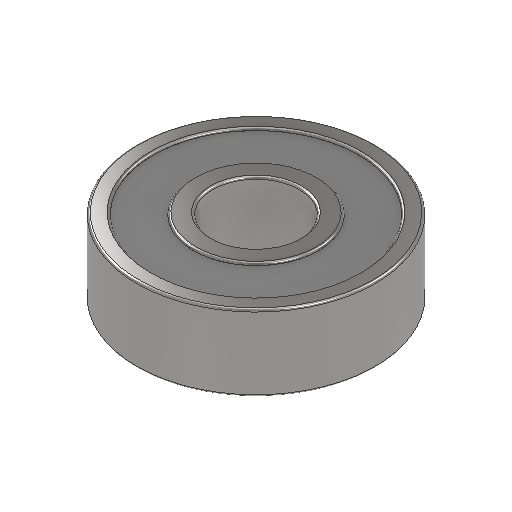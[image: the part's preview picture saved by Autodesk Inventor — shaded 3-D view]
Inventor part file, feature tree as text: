
AUTODESK INVENTOR PART (.ipt)
format: ipt  version: 2025 (Build 290162000, 162)  size: 207,360 bytes
history: native  units: in
note: dims shown in document units (in); Inventor stores cm internally (conversion verified against a paired STEP export)
features: extrude x2, fillet x2, sketch x2, plane x1, mirror x1, projected_geometry x1
ambient origin geometry x8: Origin, YZ Plane, XZ Plane, XY Plane, X Axis, Y Axis, Z Axis, Center Point
bodies: Solid1 (feature_tree)
feature tree (9):
  extrude  "Extrusion1"  Depth=0.315in
  extrude  "Extrusion2"  Depth=0.0079in
  fillet  "Fillet1"  Radius=0.4528in
  plane  "Work Plane1"
  mirror  "Mirror2"
  fillet  "Fillet2"  Radius=0.0083in
  sketch  "Sketch1"  dims[d0=0.8661in d1=0.315in]
  sketch  "Sketch2"  dims[d2=0.2756in d3=0.0in d4=0.748in d5=0.4528in d6=0.0083in d7=0.0in d8=0.0079in d9=0.0079in]
  projected_geometry  "Projected Loop1"
